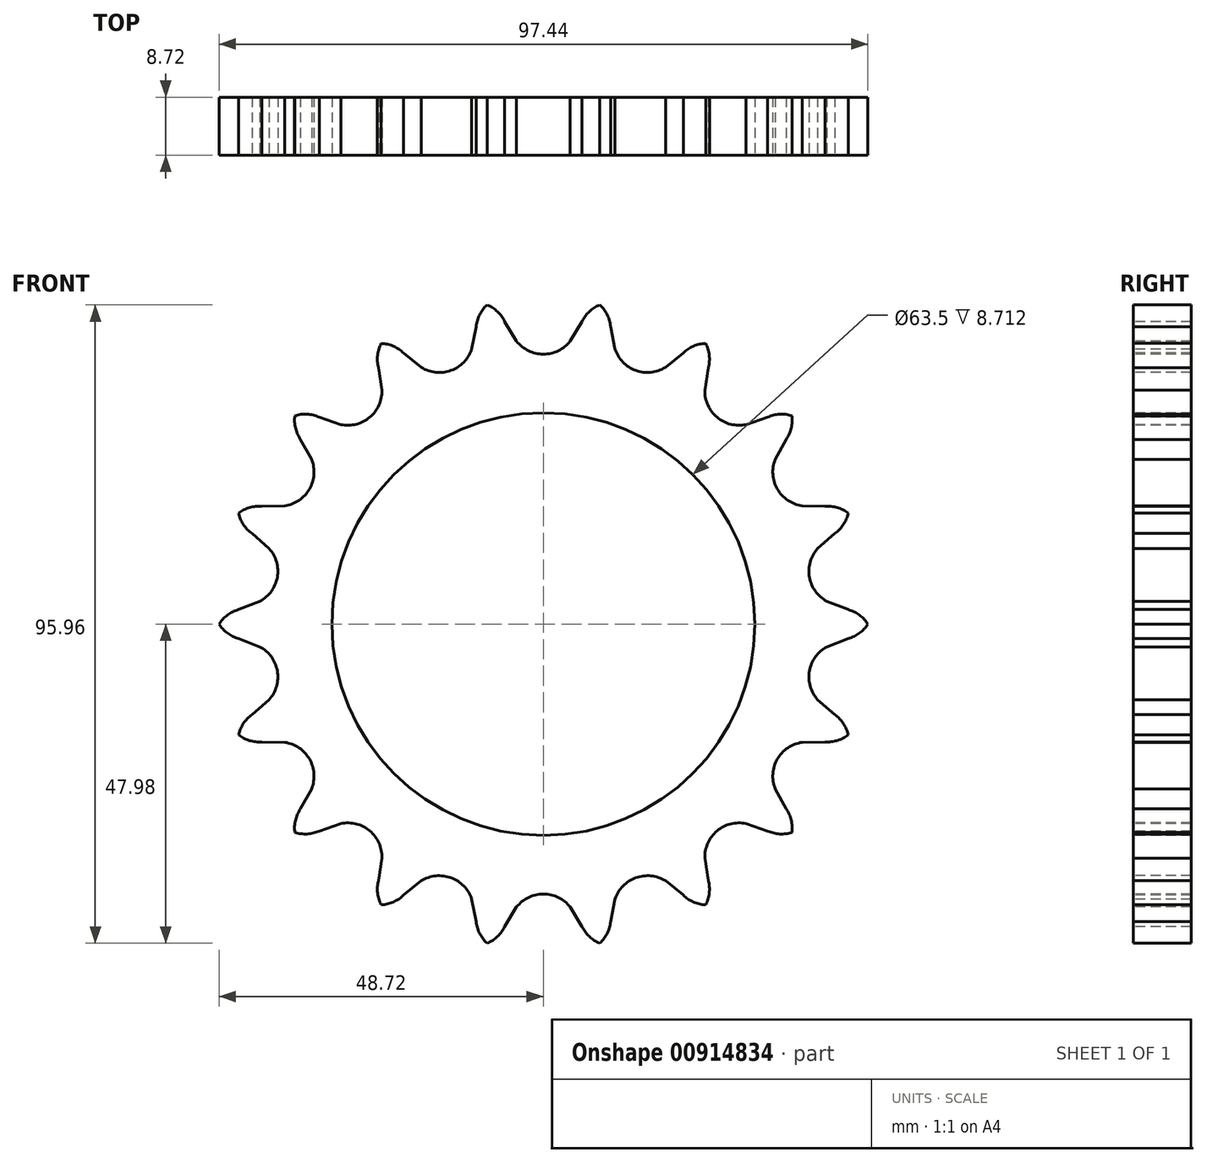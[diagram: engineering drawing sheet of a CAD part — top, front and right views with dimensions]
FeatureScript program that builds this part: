
annotation { "Feature Type Name" : "Feature", "Feature Type Description" : "" }
export const myFeature = defineFeature(function(context is Context, id is Id, definition is map)
    precondition{}
    {
        {
            var Q0;
            Q0=qCreatedBy(makeId("Front.planeOp"),FACE);
            var sketch = newSketch(context, id + "F0", { "sketchPlane" : qUnion([Q0])});
            skCircle(sketch, "E0", {"center": v(0, 0) * mm, "radius": 49.78 * mm});
            skSolve(sketch);
        }
        {
            var Q0;
            Q0 = qSketchRegion(id + "F0", true);
            extrude(context, id + "F1", {"entities" : qUnion([Q0]), "endBound" : BoundingType.SYMMETRIC, "depth" : 8.71 * mm, "offsetDistance" : 25.4 * mm});
        }
        {
            var Q0;
            Q0=makeQuery(id+"F1.opExtrude","CAP_FACE",FACE,{"disambiguationData":[OSD([sQuery(id+"F0.wireOp",EDGE,"E0")])],"isStart":false});
            var sketch = newSketch(context, id + "F2", { "sketchPlane" : qUnion([Q0])});
            skCircle(sketch, "E1", {"center": v(0, 0) * mm, "radius": 31.75 * mm});
            skSolve(sketch);
        }
        {
            var Q0;
            Q0=makeQuery(id+"F2.imprint","IMPRINT",FACE,{"disambiguationData":[TD([[makeQuery(id+"F2.imprint","IMPRINT",EDGE,{"derivedFrom":sQuery(id+"F2.wireOp",EDGE,"E1")}),1.0]])]});
            extrude(context, id + "F3", {"entities" : qUnion([Q0]), "operationType" : NewBodyOperationType.REMOVE, "endBound" : BoundingType.THROUGH_ALL, "oppositeDirection" : true, "depth" : 25.4 * mm, "offsetDistance" : 25.4 * mm});
        }
        {
            var Q0;
            Q0=makeQuery(id+"F1.opExtrude","CAP_FACE",FACE,{"disambiguationData":[OSD([sQuery(id+"F0.wireOp",EDGE,"E0")])],"isStart":false});
            var sketch = newSketch(context, id + "F4", { "sketchPlane" : qUnion([Q0])});
            skCircle(sketch, "E2", {"center": v(0, 0) * mm, "radius": 45.7 * mm, "construction": true});
            skLineSegment(sketch, "E3", {"start": v(0, 0) * mm, "end": v(0, 50.84) * mm, "construction": true});
            skLineSegment(sketch, "E4.0", {"start": v(6.38, 0) * mm, "end": v(6.38, 50.75) * mm, "construction": true});
            skLineSegment(sketch, "E5", {"start": v(-14.93, 45.7) * mm, "end": v(6.38, 45.7) * mm, "construction": true});
            skLineSegment(sketch, "E6.0", {"start": v(-0.97, 50.75) * mm, "end": v(6.38, 50.75) * mm, "construction": true});
            skLineSegment(sketch, "E7", {"start": v(6.38, 50.75) * mm, "end": v(-4.03, 42.53) * mm, "construction": true});
            skLineSegment(sketch, "E8", {"start": v(6.38, 50.75) * mm, "end": v(-5.8, 45.47) * mm, "construction": true});
            skLineSegment(sketch, "E9", {"start": v(-5.8, 45.47) * mm, "end": v(-5.8, 45.47) * mm});
            skLineSegment(sketch, "E10", {"start": v(0, 0) * mm, "end": v(-8.46, 47.98) * mm, "construction": true});
            skArc(sketch, "E11", {"start": v(-8.46, 47.98) * mm, "mid": v(-13.96, 39.51) * mm, "end": v(-5.8, 45.47) * mm, "construction": true});
            skArc(sketch, "E12", {"start": v(-5.8, 45.47) * mm, "mid": v(-6.9, 46.97) * mm, "end": v(-8.46, 47.98) * mm});
            skLineSegment(sketch, "E13", {"start": v(-4.27, 2.47) * mm, "end": v(-4.27, 2.47) * mm});
            skArc(sketch, "E14", {"start": v(-4.03, 42.53) * mm, "mid": v(0, 40.58) * mm, "end": v(4.03, 42.53) * mm});
            skArc(sketch, "E15", {"start": v(4.03, 42.53) * mm, "mid": v(0, 50.84) * mm, "end": v(-4.03, 42.53) * mm, "construction": true});
            skArc(sketch, "E16.MirrorCS", {"start": v(5.8, 45.47) * mm, "mid": v(6.9, 46.97) * mm, "end": v(8.46, 47.98) * mm});
            skLineSegment(sketch, "E17", {"start": v(-5.8, 45.47) * mm, "end": v(-4.03, 42.53) * mm});
            skLineSegment(sketch, "E18.MirrorCS", {"start": v(5.8, 45.47) * mm, "end": v(4.03, 42.53) * mm});
            skArc(sketch, "E19.1.0", {"start": v(-21, 40.74) * mm, "mid": v(-22.55, 41.78) * mm, "end": v(-24.36, 42.2) * mm});
            skLineSegment(sketch, "E19.1.1", {"start": v(-21, 40.74) * mm, "end": v(-18.33, 38.58) * mm});
            skArc(sketch, "E19.1.2", {"start": v(-18.33, 38.58) * mm, "mid": v(-13.88, 38.13) * mm, "end": v(-10.76, 41.34) * mm});
            skLineSegment(sketch, "E19.1.3", {"start": v(-10.1, 44.71) * mm, "end": v(-10.76, 41.34) * mm});
            skArc(sketch, "E19.1.4", {"start": v(-10.1, 44.71) * mm, "mid": v(-9.58, 46.5) * mm, "end": v(-8.46, 47.98) * mm});
            skArc(sketch, "E19.2.0", {"start": v(-33.67, 31.1) * mm, "mid": v(-35.48, 31.55) * mm, "end": v(-37.32, 31.32) * mm});
            skLineSegment(sketch, "E19.2.1", {"start": v(-33.67, 31.1) * mm, "end": v(-30.42, 29.99) * mm});
            skArc(sketch, "E19.2.2", {"start": v(-30.42, 29.99) * mm, "mid": v(-26.08, 31.08) * mm, "end": v(-24.25, 35.17) * mm});
            skLineSegment(sketch, "E19.2.3", {"start": v(-24.78, 38.56) * mm, "end": v(-24.25, 35.17) * mm});
            skArc(sketch, "E19.2.4", {"start": v(-24.78, 38.56) * mm, "mid": v(-24.9, 40.42) * mm, "end": v(-24.36, 42.2) * mm});
            skArc(sketch, "E19.3.0", {"start": v(-42.28, 17.7) * mm, "mid": v(-44.13, 17.5) * mm, "end": v(-45.78, 16.66) * mm});
            skLineSegment(sketch, "E19.3.1", {"start": v(-42.28, 17.7) * mm, "end": v(-38.84, 17.77) * mm});
            skArc(sketch, "E19.3.2", {"start": v(-38.84, 17.77) * mm, "mid": v(-35.14, 20.29) * mm, "end": v(-34.81, 24.75) * mm});
            skLineSegment(sketch, "E19.3.3", {"start": v(-36.48, 27.76) * mm, "end": v(-34.81, 24.75) * mm});
            skArc(sketch, "E19.3.4", {"start": v(-36.48, 27.76) * mm, "mid": v(-37.23, 29.46) * mm, "end": v(-37.32, 31.32) * mm});
            skArc(sketch, "E19.4.0", {"start": v(-45.79, 2.18) * mm, "mid": v(-47.46, 1.36) * mm, "end": v(-48.72, 0) * mm});
            skLineSegment(sketch, "E19.4.1", {"start": v(-45.79, 2.18) * mm, "end": v(-42.58, 3.42) * mm});
            skArc(sketch, "E19.4.2", {"start": v(-42.58, 3.42) * mm, "mid": v(-39.96, 7.05) * mm, "end": v(-41.18, 11.35) * mm});
            skLineSegment(sketch, "E19.4.3", {"start": v(-43.77, 13.61) * mm, "end": v(-41.18, 11.35) * mm});
            skArc(sketch, "E19.4.4", {"start": v(-43.77, 13.61) * mm, "mid": v(-45.06, 14.95) * mm, "end": v(-45.78, 16.66) * mm});
            skArc(sketch, "E19.5.0", {"start": v(-43.77, -13.61) * mm, "mid": v(-45.06, -14.95) * mm, "end": v(-45.78, -16.66) * mm});
            skLineSegment(sketch, "E19.5.1", {"start": v(-43.77, -13.61) * mm, "end": v(-41.18, -11.35) * mm});
            skArc(sketch, "E19.5.2", {"start": v(-41.18, -11.35) * mm, "mid": v(-39.96, -7.05) * mm, "end": v(-42.58, -3.42) * mm});
            skLineSegment(sketch, "E19.5.3", {"start": v(-45.79, -2.18) * mm, "end": v(-42.58, -3.42) * mm});
            skArc(sketch, "E19.5.4", {"start": v(-45.79, -2.18) * mm, "mid": v(-47.46, -1.36) * mm, "end": v(-48.72, 0) * mm});
            skArc(sketch, "E19.6.0", {"start": v(-36.48, -27.76) * mm, "mid": v(-37.23, -29.46) * mm, "end": v(-37.32, -31.32) * mm});
            skLineSegment(sketch, "E19.6.1", {"start": v(-36.48, -27.76) * mm, "end": v(-34.81, -24.75) * mm});
            skArc(sketch, "E19.6.2", {"start": v(-34.81, -24.75) * mm, "mid": v(-35.14, -20.29) * mm, "end": v(-38.84, -17.77) * mm});
            skLineSegment(sketch, "E19.6.3", {"start": v(-42.28, -17.7) * mm, "end": v(-38.84, -17.77) * mm});
            skArc(sketch, "E19.6.4", {"start": v(-42.28, -17.7) * mm, "mid": v(-44.13, -17.5) * mm, "end": v(-45.78, -16.66) * mm});
            skArc(sketch, "E19.7.0", {"start": v(-24.78, -38.56) * mm, "mid": v(-24.9, -40.42) * mm, "end": v(-24.36, -42.2) * mm});
            skLineSegment(sketch, "E19.7.1", {"start": v(-24.78, -38.56) * mm, "end": v(-24.25, -35.17) * mm});
            skArc(sketch, "E19.7.2", {"start": v(-24.25, -35.17) * mm, "mid": v(-26.08, -31.08) * mm, "end": v(-30.42, -29.99) * mm});
            skLineSegment(sketch, "E19.7.3", {"start": v(-33.67, -31.1) * mm, "end": v(-30.42, -29.99) * mm});
            skArc(sketch, "E19.7.4", {"start": v(-33.67, -31.1) * mm, "mid": v(-35.48, -31.55) * mm, "end": v(-37.32, -31.32) * mm});
            skArc(sketch, "E19.8.0", {"start": v(-10.1, -44.71) * mm, "mid": v(-9.58, -46.5) * mm, "end": v(-8.46, -47.98) * mm});
            skLineSegment(sketch, "E19.8.1", {"start": v(-10.1, -44.71) * mm, "end": v(-10.76, -41.34) * mm});
            skArc(sketch, "E19.8.2", {"start": v(-10.76, -41.34) * mm, "mid": v(-13.88, -38.13) * mm, "end": v(-18.33, -38.58) * mm});
            skLineSegment(sketch, "E19.8.3", {"start": v(-21, -40.74) * mm, "end": v(-18.33, -38.58) * mm});
            skArc(sketch, "E19.8.4", {"start": v(-21, -40.74) * mm, "mid": v(-22.55, -41.78) * mm, "end": v(-24.36, -42.2) * mm});
            skArc(sketch, "E19.9.0", {"start": v(5.8, -45.47) * mm, "mid": v(6.9, -46.97) * mm, "end": v(8.46, -47.98) * mm});
            skLineSegment(sketch, "E19.9.1", {"start": v(5.8, -45.47) * mm, "end": v(4.03, -42.53) * mm});
            skArc(sketch, "E19.9.2", {"start": v(4.03, -42.53) * mm, "mid": v(0, -40.58) * mm, "end": v(-4.03, -42.53) * mm});
            skLineSegment(sketch, "E19.9.3", {"start": v(-5.8, -45.47) * mm, "end": v(-4.03, -42.53) * mm});
            skArc(sketch, "E19.9.4", {"start": v(-5.8, -45.47) * mm, "mid": v(-6.9, -46.97) * mm, "end": v(-8.46, -47.98) * mm});
            skArc(sketch, "E19.10.0", {"start": v(21, -40.74) * mm, "mid": v(22.55, -41.78) * mm, "end": v(24.36, -42.2) * mm});
            skLineSegment(sketch, "E19.10.1", {"start": v(21, -40.74) * mm, "end": v(18.33, -38.58) * mm});
            skArc(sketch, "E19.10.2", {"start": v(18.33, -38.58) * mm, "mid": v(13.88, -38.13) * mm, "end": v(10.76, -41.34) * mm});
            skLineSegment(sketch, "E19.10.3", {"start": v(10.1, -44.71) * mm, "end": v(10.76, -41.34) * mm});
            skArc(sketch, "E19.10.4", {"start": v(10.1, -44.71) * mm, "mid": v(9.58, -46.5) * mm, "end": v(8.46, -47.98) * mm});
            skArc(sketch, "E19.11.0", {"start": v(33.67, -31.1) * mm, "mid": v(35.48, -31.55) * mm, "end": v(37.32, -31.32) * mm});
            skLineSegment(sketch, "E19.11.1", {"start": v(33.67, -31.1) * mm, "end": v(30.42, -29.99) * mm});
            skArc(sketch, "E19.11.2", {"start": v(30.42, -29.99) * mm, "mid": v(26.08, -31.08) * mm, "end": v(24.25, -35.17) * mm});
            skLineSegment(sketch, "E19.11.3", {"start": v(24.78, -38.56) * mm, "end": v(24.25, -35.17) * mm});
            skArc(sketch, "E19.11.4", {"start": v(24.78, -38.56) * mm, "mid": v(24.9, -40.42) * mm, "end": v(24.36, -42.2) * mm});
            skArc(sketch, "E19.12.0", {"start": v(42.28, -17.7) * mm, "mid": v(44.13, -17.5) * mm, "end": v(45.78, -16.66) * mm});
            skLineSegment(sketch, "E19.12.1", {"start": v(42.28, -17.7) * mm, "end": v(38.84, -17.77) * mm});
            skArc(sketch, "E19.12.2", {"start": v(38.84, -17.77) * mm, "mid": v(35.14, -20.29) * mm, "end": v(34.81, -24.75) * mm});
            skLineSegment(sketch, "E19.12.3", {"start": v(36.48, -27.76) * mm, "end": v(34.81, -24.75) * mm});
            skArc(sketch, "E19.12.4", {"start": v(36.48, -27.76) * mm, "mid": v(37.23, -29.46) * mm, "end": v(37.32, -31.32) * mm});
            skArc(sketch, "E19.13.0", {"start": v(45.79, -2.18) * mm, "mid": v(47.46, -1.36) * mm, "end": v(48.72, 0) * mm});
            skLineSegment(sketch, "E19.13.1", {"start": v(45.79, -2.18) * mm, "end": v(42.58, -3.42) * mm});
            skArc(sketch, "E19.13.2", {"start": v(42.58, -3.42) * mm, "mid": v(39.96, -7.05) * mm, "end": v(41.18, -11.35) * mm});
            skLineSegment(sketch, "E19.13.3", {"start": v(43.77, -13.61) * mm, "end": v(41.18, -11.35) * mm});
            skArc(sketch, "E19.13.4", {"start": v(43.77, -13.61) * mm, "mid": v(45.06, -14.95) * mm, "end": v(45.78, -16.66) * mm});
            skArc(sketch, "E19.14.0", {"start": v(43.77, 13.61) * mm, "mid": v(45.06, 14.95) * mm, "end": v(45.78, 16.66) * mm});
            skLineSegment(sketch, "E19.14.1", {"start": v(43.77, 13.61) * mm, "end": v(41.18, 11.35) * mm});
            skArc(sketch, "E19.14.2", {"start": v(41.18, 11.35) * mm, "mid": v(39.96, 7.05) * mm, "end": v(42.58, 3.42) * mm});
            skLineSegment(sketch, "E19.14.3", {"start": v(45.79, 2.18) * mm, "end": v(42.58, 3.42) * mm});
            skArc(sketch, "E19.14.4", {"start": v(45.79, 2.18) * mm, "mid": v(47.46, 1.36) * mm, "end": v(48.72, 0) * mm});
            skArc(sketch, "E19.15.0", {"start": v(36.48, 27.76) * mm, "mid": v(37.23, 29.46) * mm, "end": v(37.32, 31.32) * mm});
            skLineSegment(sketch, "E19.15.1", {"start": v(36.48, 27.76) * mm, "end": v(34.81, 24.75) * mm});
            skArc(sketch, "E19.15.2", {"start": v(34.81, 24.75) * mm, "mid": v(35.14, 20.29) * mm, "end": v(38.84, 17.77) * mm});
            skLineSegment(sketch, "E19.15.3", {"start": v(42.28, 17.7) * mm, "end": v(38.84, 17.77) * mm});
            skArc(sketch, "E19.15.4", {"start": v(42.28, 17.7) * mm, "mid": v(44.13, 17.5) * mm, "end": v(45.78, 16.66) * mm});
            skArc(sketch, "E19.16.0", {"start": v(24.78, 38.56) * mm, "mid": v(24.9, 40.42) * mm, "end": v(24.36, 42.2) * mm});
            skLineSegment(sketch, "E19.16.1", {"start": v(24.78, 38.56) * mm, "end": v(24.25, 35.17) * mm});
            skArc(sketch, "E19.16.2", {"start": v(24.25, 35.17) * mm, "mid": v(26.08, 31.08) * mm, "end": v(30.42, 29.99) * mm});
            skLineSegment(sketch, "E19.16.3", {"start": v(33.67, 31.1) * mm, "end": v(30.42, 29.99) * mm});
            skArc(sketch, "E19.16.4", {"start": v(33.67, 31.1) * mm, "mid": v(35.48, 31.55) * mm, "end": v(37.32, 31.32) * mm});
            skArc(sketch, "E19.17.0", {"start": v(10.1, 44.71) * mm, "mid": v(9.58, 46.5) * mm, "end": v(8.46, 47.98) * mm});
            skLineSegment(sketch, "E19.17.1", {"start": v(10.1, 44.71) * mm, "end": v(10.76, 41.34) * mm});
            skArc(sketch, "E19.17.2", {"start": v(10.76, 41.34) * mm, "mid": v(13.88, 38.13) * mm, "end": v(18.33, 38.58) * mm});
            skLineSegment(sketch, "E19.17.3", {"start": v(21, 40.74) * mm, "end": v(18.33, 38.58) * mm});
            skArc(sketch, "E19.17.4", {"start": v(21, 40.74) * mm, "mid": v(22.55, 41.78) * mm, "end": v(24.36, 42.2) * mm});
            skSolve(sketch);
        }
        {
            var Q0;
            Q0=makeQuery(id+"F4.imprint","IMPRINT",FACE,{"disambiguationData":[TD([[makeQuery(id+"F4.imprint","IMPRINT",EDGE,{"derivedFrom":sQuery(id+"F4.wireOp",EDGE,"E12")}),1.0]])]});
            extrude(context, id + "F5", {"entities" : qUnion([Q0]), "operationType" : NewBodyOperationType.INTERSECT, "endBound" : BoundingType.THROUGH_ALL, "oppositeDirection" : true, "depth" : 25.4 * mm, "offsetDistance" : 25.4 * mm});
        }
    });
